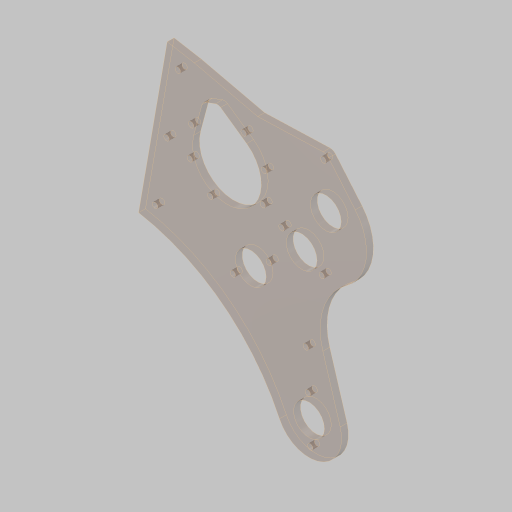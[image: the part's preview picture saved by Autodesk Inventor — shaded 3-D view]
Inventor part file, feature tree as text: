
AUTODESK INVENTOR PART (.ipt)
format: ipt  version: 2023.5 (Build 275446000, 446)  size: 314,368 bytes
history: native  units: in
note: dims shown in document units (in); Inventor stores cm internally (conversion verified against a paired STEP export)
features: sketch x5, extrude x3, hole x3, projected_geometry x3, fillet x1
ambient origin geometry x8: Origin, YZ Plane, XZ Plane, XY Plane, X Axis, Y Axis, Z Axis, Center Point
bodies: Solid1 (feature_tree)
feature tree (15):
  sketch  "Sketch1"  dims[d3=45.0deg d4=0.0in]
  extrude  "Extrusion1"  TaperAngle=0.0deg  [1 undecoded]
  hole  "Hole1"  [1 undecoded]
  hole  "Hole2"  [1 undecoded]
  extrude  "Extrusion3"  Depth=4.5in
  fillet  "Fillet2"  Radius=0.625in
  extrude  "Extrusion4"  Depth=0.25in
  hole  "Hole3"  [1 undecoded]
  sketch  "Sketch2"  dims[d7=4.0in d8=4.0in]
  projected_geometry  "Projected Loop1"
  sketch  "Sketch4"  dims[d9=1.123in d10=4.0in]
  projected_geometry  "Projected Loop2"
  sketch  "Sketch5"  dims[d11=4.5in d12=4.5in d13=0.625in]
  sketch  "Sketch6"  dims[d14=0.625in d15=5.181in d16=1.128in d17=5.181in d18=1.8765in d19=1.8765in d22=1.0in d23=6.0in d26=10.5532in d27=2.5in d30=8.0in d31=0.0687in d32=0.75in d33=4.75in d34=1.375in d35=0.75in d36=0.25in d38=2.3622in d40=360.0deg d44=0.375in d45=0.25in d46=0.0in d47=0.201in d48=0.75in d49=0.37in d50=0.25in d51=90.0deg d52=1.0in d53=0.8108in d55=0.5497in d56=0.3in d57=0.25in d58=2.256in d59=2.5in d60=2.9555in d61=2.35in d62=0.3779in d65=2.0in d66=2.3622in d68=360.0deg d70=1.625in d71=60.0deg d72=1.655in d73=0.201in d74=0.75in d75=0.385in d76=0.25in d77=0.5635in d78=1.0in d79=0.8108in d86=1.5748in d88=360.0deg d91=1.5748in d93=360.0deg d95=45.0deg d96=1.75in d98=0.8589in d99=0.0in d100=0.0in d101=0.2in d102=1.75in d103=5.75in d104=0.375in d105=0.5in d106=15.0deg d107=0.25in d108=0.0in d109=0.201in d110=0.75in d111=0.385in d112=0.25in d113=0.5635in d114=1.0in d115=0.8108in d116=0.875in]
  projected_geometry  "Projected Loop3"
note: 4 required parameter values undecoded (feature->parameter linkage not recoverable at this tier; creation-order binding heuristic only, values carry confidence <= 0.55)
